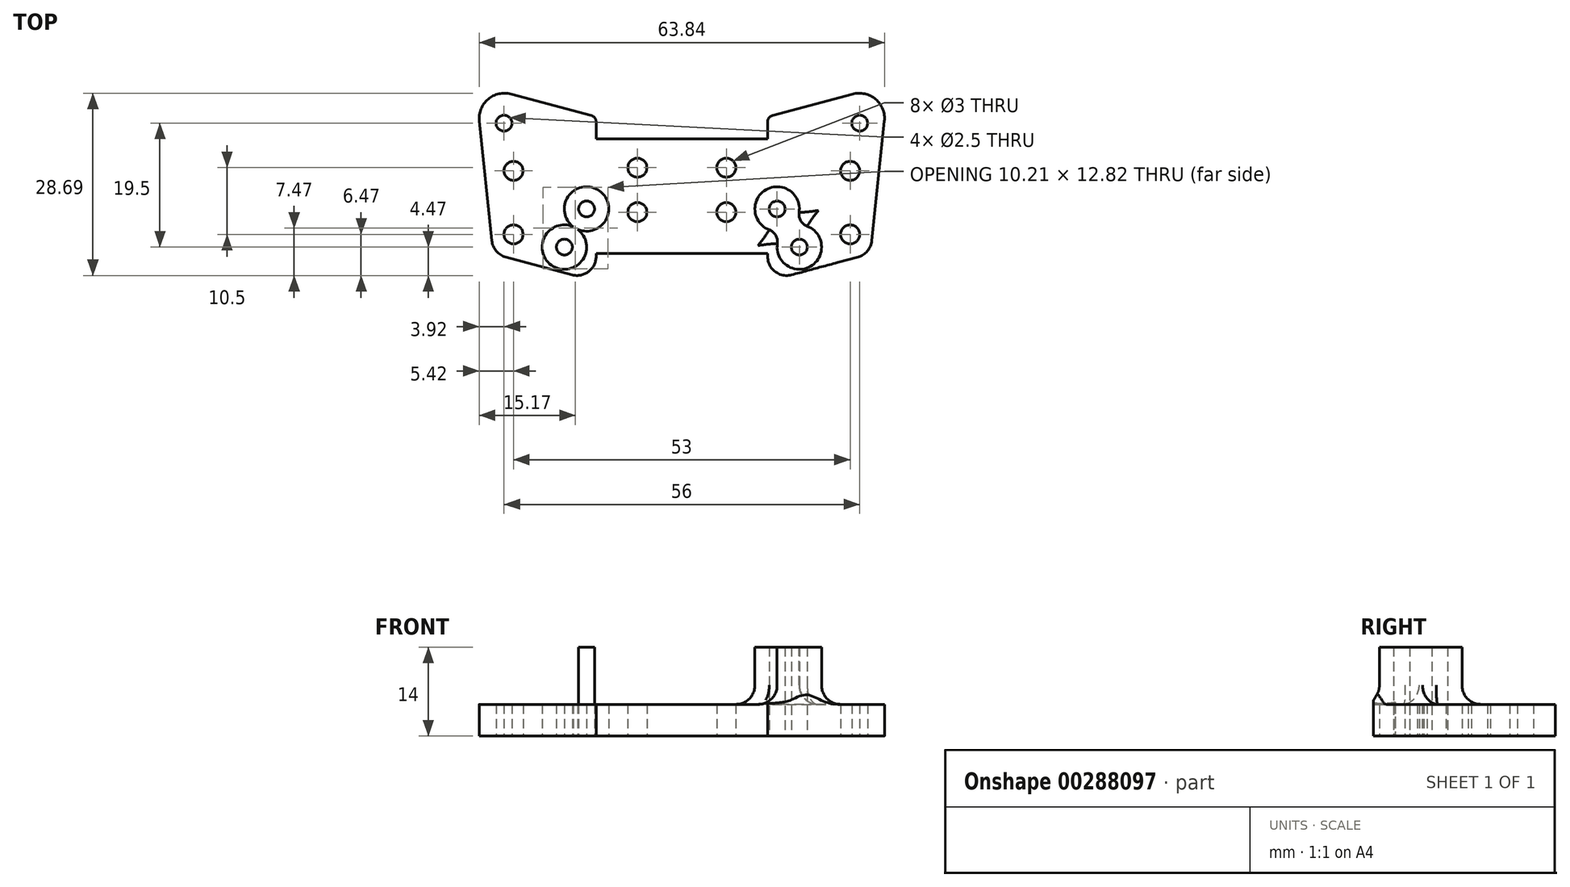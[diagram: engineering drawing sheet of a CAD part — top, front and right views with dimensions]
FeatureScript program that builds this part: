
annotation { "Feature Type Name" : "Feature", "Feature Type Description" : "" }
export const myFeature = defineFeature(function(context is Context, id is Id, definition is map)
    precondition{}
    {
        {
            var Q0;
            Q0=qCreatedBy(makeId("Top.planeOp"),FACE);
            var sketch = newSketch(context, id + "F0", { "sketchPlane" : qUnion([Q0])});
            skLineSegment(sketch, "E0", {"start": v(0, 0) * mm, "end": v(0, 21.8) * mm, "construction": true});
            skLineSegment(sketch, "E1", {"start": v(0, 0) * mm, "end": v(13.5, 0) * mm});
            skLineSegment(sketch, "E2", {"start": v(13.5, 0) * mm, "end": v(13.5, 2.73) * mm});
            skLineSegment(sketch, "E3", {"start": v(14.24, 3.7) * mm, "end": v(26.88, 7.09) * mm});
            skLineSegment(sketch, "E4", {"start": v(31.9, 2.8) * mm, "end": v(29.92, -15.99) * mm});
            skLineSegment(sketch, "E5", {"start": v(27.71, -18.57) * mm, "end": v(17.28, -21.37) * mm});
            skLineSegment(sketch, "E6", {"start": v(13.5, -18.47) * mm, "end": v(13.5, -18) * mm});
            skLineSegment(sketch, "E7", {"start": v(13.5, -18) * mm, "end": v(0, -18) * mm});
            skLineSegment(sketch, "E8", {"start": v(32.5, 8.6) * mm, "end": v(32.5, -12.43) * mm, "construction": true});
            skCircle(sketch, "E9", {"center": v(28, 2.5) * mm, "radius": 1.25 * mm});
            skPoint(sketch, "E10.visualSharp", {"position": v(32.5, 8.6) * mm});
            skArc(sketch, "E10.filletArc", {"start": v(31.9, 2.8) * mm, "mid": v(30.51, 6.26) * mm, "end": v(26.88, 7.09) * mm});
            skCircle(sketch, "E11", {"center": v(26.5, -5) * mm, "radius": 1.5 * mm});
            skCircle(sketch, "E12", {"center": v(26.5, -15) * mm, "radius": 1.5 * mm});
            skCircle(sketch, "E13", {"center": v(7, -4.5) * mm, "radius": 1.5 * mm});
            skCircle(sketch, "E14", {"center": v(7, -11.5) * mm, "radius": 1.5 * mm});
            skCircle(sketch, "E15", {"center": v(15, -11) * mm, "radius": 1.25 * mm});
            skCircle(sketch, "E16", {"center": v(18.5, -17) * mm, "radius": 1.25 * mm});
            skArc(sketch, "E17", {"start": v(17.12, -13.78) * mm, "mid": v(13.24, -7.98) * mm, "end": v(16.38, -14.22) * mm});
            skArc(sketch, "E18", {"start": v(16.38, -14.22) * mm, "mid": v(20.26, -20.02) * mm, "end": v(17.12, -13.78) * mm});
            skPoint(sketch, "E19.visualSharp", {"position": v(13.5, 3.5) * mm});
            skArc(sketch, "E19.filletArc", {"start": v(14.24, 3.7) * mm, "mid": v(13.7, 3.34) * mm, "end": v(13.5, 2.73) * mm});
            skPoint(sketch, "E20.visualSharp", {"position": v(29.7, -18.04) * mm});
            skArc(sketch, "E20.filletArc", {"start": v(27.71, -18.57) * mm, "mid": v(29.22, -17.62) * mm, "end": v(29.92, -15.99) * mm});
            skPoint(sketch, "E21.visualSharp", {"position": v(13.5, -22.38) * mm});
            skArc(sketch, "E21.filletArc", {"start": v(13.5, -18.47) * mm, "mid": v(14.67, -20.85) * mm, "end": v(17.28, -21.37) * mm});
            skCircle(sketch, "E22.MirrorC", {"center": v(-7, -4.5) * mm, "radius": 1.5 * mm});
            skCircle(sketch, "E23.MirrorC", {"center": v(-7, -11.5) * mm, "radius": 1.5 * mm});
            skCircle(sketch, "E24.MirrorC", {"center": v(-15, -11) * mm, "radius": 1.25 * mm});
            skArc(sketch, "E25.MirrorC", {"start": v(-17.12, -13.78) * mm, "mid": v(-13.24, -7.98) * mm, "end": v(-16.38, -14.22) * mm});
            skCircle(sketch, "E26.MirrorC", {"center": v(-18.5, -17) * mm, "radius": 1.25 * mm});
            skArc(sketch, "E27.MirrorC", {"start": v(-16.38, -14.22) * mm, "mid": v(-20.26, -20.02) * mm, "end": v(-17.12, -13.78) * mm});
            skCircle(sketch, "E28.MirrorC", {"center": v(-26.5, -15) * mm, "radius": 1.5 * mm});
            skCircle(sketch, "E29.MirrorC", {"center": v(-26.5, -5) * mm, "radius": 1.5 * mm});
            skCircle(sketch, "E30.MirrorC", {"center": v(-28, 2.5) * mm, "radius": 1.25 * mm});
            skLineSegment(sketch, "E31.MirrorCS", {"start": v(-13.5, -18) * mm, "end": v(0, -18) * mm});
            skLineSegment(sketch, "E32.MirrorCS", {"start": v(-13.5, -18.47) * mm, "end": v(-13.5, -18) * mm});
            skArc(sketch, "E33.MirrorCS", {"start": v(-13.5, -18.47) * mm, "mid": v(-14.67, -20.85) * mm, "end": v(-17.28, -21.37) * mm});
            skLineSegment(sketch, "E34.MirrorCS", {"start": v(-27.71, -18.57) * mm, "end": v(-17.28, -21.37) * mm});
            skArc(sketch, "E35.MirrorCS", {"start": v(-27.71, -18.57) * mm, "mid": v(-29.22, -17.62) * mm, "end": v(-29.92, -15.99) * mm});
            skLineSegment(sketch, "E36.MirrorCS", {"start": v(-31.9, 2.8) * mm, "end": v(-29.92, -15.99) * mm});
            skArc(sketch, "E37.MirrorCS", {"start": v(-31.9, 2.8) * mm, "mid": v(-30.51, 6.26) * mm, "end": v(-26.88, 7.09) * mm});
            skLineSegment(sketch, "E38.MirrorCS", {"start": v(-14.24, 3.7) * mm, "end": v(-26.88, 7.09) * mm});
            skArc(sketch, "E39.MirrorCS", {"start": v(-14.24, 3.7) * mm, "mid": v(-13.7, 3.34) * mm, "end": v(-13.5, 2.73) * mm});
            skLineSegment(sketch, "E40.MirrorCS", {"start": v(0, 0) * mm, "end": v(-13.5, 0) * mm});
            skLineSegment(sketch, "E41.MirrorCS", {"start": v(-13.5, 0) * mm, "end": v(-13.5, 2.73) * mm});
            skSolve(sketch);
        }
        {
            var Q0;
            Q0=makeQuery(id+"F0.imprint","IMPRINT",FACE,{"disambiguationData":[TD([[makeQuery(id+"F0.imprint","IMPRINT",EDGE,{"derivedFrom":sQuery(id+"F0.wireOp",EDGE,"E1")}),-1.0]])]});
            var Q1;
            Q1=makeQuery(id+"F0.imprint","IMPRINT",FACE,{"disambiguationData":[TD([[makeQuery(id+"F0.imprint","IMPRINT",EDGE,{"derivedFrom":sQuery(id+"F0.wireOp",EDGE,"E15")}),-1.0]])]});
            var Q2;
            Q2=makeQuery(id+"F0.imprint","IMPRINT",FACE,{"disambiguationData":[TD([[makeQuery(id+"F0.imprint","IMPRINT",EDGE,{"derivedFrom":sQuery(id+"F0.wireOp",EDGE,"E16")}),-1.0]])]});
            var Q3;
            Q3=makeQuery(id+"F0.imprint","IMPRINT",FACE,{"disambiguationData":[TD([[makeQuery(id+"F0.imprint","IMPRINT",EDGE,{"derivedFrom":sQuery(id+"F0.wireOp",EDGE,"E24.MirrorC")}),1.0]])]});
            var Q4;
            Q4=makeQuery(id+"F0.imprint","IMPRINT",FACE,{"disambiguationData":[TD([[makeQuery(id+"F0.imprint","IMPRINT",EDGE,{"derivedFrom":sQuery(id+"F0.wireOp",EDGE,"E26.MirrorC")}),1.0]])]});
            extrude(context, id + "F1", {"entities" : qUnion([Q0, Q1, Q2, Q3, Q4]), "depth" : 5 * mm});
        }
        {
            var Q0;
            Q0=makeQuery(id+"F0.imprint","IMPRINT",FACE,{"disambiguationData":[TD([[makeQuery(id+"F0.imprint","IMPRINT",EDGE,{"derivedFrom":sQuery(id+"F0.wireOp",EDGE,"E24.MirrorC")}),1.0]])]});
            var Q1;
            Q1=makeQuery(id+"F0.imprint","IMPRINT",FACE,{"disambiguationData":[TD([[makeQuery(id+"F0.imprint","IMPRINT",EDGE,{"derivedFrom":sQuery(id+"F0.wireOp",EDGE,"E15")}),-1.0]])]});
            extrude(context, id + "F2", {"entities" : qUnion([Q0, Q1]), "operationType" : NewBodyOperationType.ADD, "depth" : 14 * mm});
        }
        {
            var Q0;
            Q0=makeQuery(id+"F2.boolean.opBoolean","INTERSECT",EDGE,{"derivedFrom":[makeQuery(id+"F1.opExtrude","CAP_FACE",FACE,{"disambiguationData":[OSD([sQuery(id+"F0.wireOp",EDGE,"E1"),sQuery(id+"F0.wireOp",EDGE,"E2"),sQuery(id+"F0.wireOp",EDGE,"E3"),sQuery(id+"F0.wireOp",EDGE,"E4"),sQuery(id+"F0.wireOp",EDGE,"E5"),sQuery(id+"F0.wireOp",EDGE,"E6"),sQuery(id+"F0.wireOp",EDGE,"E7"),sQuery(id+"F0.wireOp",EDGE,"E9"),sQuery(id+"F0.wireOp",EDGE,"E10.filletArc"),sQuery(id+"F0.wireOp",EDGE,"E11"),sQuery(id+"F0.wireOp",EDGE,"E12"),sQuery(id+"F0.wireOp",EDGE,"E13"),sQuery(id+"F0.wireOp",EDGE,"E14"),sQuery(id+"F0.wireOp",EDGE,"E15"),sQuery(id+"F0.wireOp",EDGE,"E16"),sQuery(id+"F0.wireOp",EDGE,"E19.filletArc"),sQuery(id+"F0.wireOp",EDGE,"E20.filletArc"),sQuery(id+"F0.wireOp",EDGE,"E21.filletArc"),sQuery(id+"F0.wireOp",EDGE,"E22.MirrorC"),sQuery(id+"F0.wireOp",EDGE,"E23.MirrorC"),sQuery(id+"F0.wireOp",EDGE,"E24.MirrorC"),sQuery(id+"F0.wireOp",EDGE,"E26.MirrorC"),sQuery(id+"F0.wireOp",EDGE,"E28.MirrorC"),sQuery(id+"F0.wireOp",EDGE,"E29.MirrorC"),sQuery(id+"F0.wireOp",EDGE,"E30.MirrorC"),sQuery(id+"F0.wireOp",EDGE,"E31.MirrorCS"),sQuery(id+"F0.wireOp",EDGE,"E32.MirrorCS"),sQuery(id+"F0.wireOp",EDGE,"E33.MirrorCS"),sQuery(id+"F0.wireOp",EDGE,"E34.MirrorCS"),sQuery(id+"F0.wireOp",EDGE,"E35.MirrorCS"),sQuery(id+"F0.wireOp",EDGE,"E36.MirrorCS"),sQuery(id+"F0.wireOp",EDGE,"E37.MirrorCS"),sQuery(id+"F0.wireOp",EDGE,"E38.MirrorCS"),sQuery(id+"F0.wireOp",EDGE,"E39.MirrorCS"),sQuery(id+"F0.wireOp",EDGE,"E40.MirrorCS"),sQuery(id+"F0.wireOp",EDGE,"E41.MirrorCS")])],"isStart":false}),makeQuery(id+"F2.opExtrude","SWEPT_FACE",FACE,{"disambiguationData":[OSD([sQuery(id+"F0.wireOp",EDGE,"E25.MirrorC")])]})]});
            var Q1;
            Q1=makeQuery(id+"F2.boolean.opBoolean","INTERSECT",EDGE,{"derivedFrom":[makeQuery(id+"F1.opExtrude","CAP_FACE",FACE,{"disambiguationData":[OSD([sQuery(id+"F0.wireOp",EDGE,"E1"),sQuery(id+"F0.wireOp",EDGE,"E2"),sQuery(id+"F0.wireOp",EDGE,"E3"),sQuery(id+"F0.wireOp",EDGE,"E4"),sQuery(id+"F0.wireOp",EDGE,"E5"),sQuery(id+"F0.wireOp",EDGE,"E6"),sQuery(id+"F0.wireOp",EDGE,"E7"),sQuery(id+"F0.wireOp",EDGE,"E9"),sQuery(id+"F0.wireOp",EDGE,"E10.filletArc"),sQuery(id+"F0.wireOp",EDGE,"E11"),sQuery(id+"F0.wireOp",EDGE,"E12"),sQuery(id+"F0.wireOp",EDGE,"E13"),sQuery(id+"F0.wireOp",EDGE,"E14"),sQuery(id+"F0.wireOp",EDGE,"E15"),sQuery(id+"F0.wireOp",EDGE,"E16"),sQuery(id+"F0.wireOp",EDGE,"E19.filletArc"),sQuery(id+"F0.wireOp",EDGE,"E20.filletArc"),sQuery(id+"F0.wireOp",EDGE,"E21.filletArc"),sQuery(id+"F0.wireOp",EDGE,"E22.MirrorC"),sQuery(id+"F0.wireOp",EDGE,"E23.MirrorC"),sQuery(id+"F0.wireOp",EDGE,"E24.MirrorC"),sQuery(id+"F0.wireOp",EDGE,"E26.MirrorC"),sQuery(id+"F0.wireOp",EDGE,"E28.MirrorC"),sQuery(id+"F0.wireOp",EDGE,"E29.MirrorC"),sQuery(id+"F0.wireOp",EDGE,"E30.MirrorC"),sQuery(id+"F0.wireOp",EDGE,"E31.MirrorCS"),sQuery(id+"F0.wireOp",EDGE,"E32.MirrorCS"),sQuery(id+"F0.wireOp",EDGE,"E33.MirrorCS"),sQuery(id+"F0.wireOp",EDGE,"E34.MirrorCS"),sQuery(id+"F0.wireOp",EDGE,"E35.MirrorCS"),sQuery(id+"F0.wireOp",EDGE,"E36.MirrorCS"),sQuery(id+"F0.wireOp",EDGE,"E37.MirrorCS"),sQuery(id+"F0.wireOp",EDGE,"E38.MirrorCS"),sQuery(id+"F0.wireOp",EDGE,"E39.MirrorCS"),sQuery(id+"F0.wireOp",EDGE,"E40.MirrorCS"),sQuery(id+"F0.wireOp",EDGE,"E41.MirrorCS")])],"isStart":false}),makeQuery(id+"F2.opExtrude","SWEPT_FACE",FACE,{"disambiguationData":[OSD([sQuery(id+"F0.wireOp",EDGE,"E27.MirrorC")])]})]});
            var Q2;
            Q2=makeQuery(id+"F2.boolean.opBoolean","INTERSECT",EDGE,{"derivedFrom":[makeQuery(id+"F1.opExtrude","CAP_FACE",FACE,{"disambiguationData":[OSD([sQuery(id+"F0.wireOp",EDGE,"E1"),sQuery(id+"F0.wireOp",EDGE,"E2"),sQuery(id+"F0.wireOp",EDGE,"E3"),sQuery(id+"F0.wireOp",EDGE,"E4"),sQuery(id+"F0.wireOp",EDGE,"E5"),sQuery(id+"F0.wireOp",EDGE,"E6"),sQuery(id+"F0.wireOp",EDGE,"E7"),sQuery(id+"F0.wireOp",EDGE,"E9"),sQuery(id+"F0.wireOp",EDGE,"E10.filletArc"),sQuery(id+"F0.wireOp",EDGE,"E11"),sQuery(id+"F0.wireOp",EDGE,"E12"),sQuery(id+"F0.wireOp",EDGE,"E13"),sQuery(id+"F0.wireOp",EDGE,"E14"),sQuery(id+"F0.wireOp",EDGE,"E15"),sQuery(id+"F0.wireOp",EDGE,"E16"),sQuery(id+"F0.wireOp",EDGE,"E19.filletArc"),sQuery(id+"F0.wireOp",EDGE,"E20.filletArc"),sQuery(id+"F0.wireOp",EDGE,"E21.filletArc"),sQuery(id+"F0.wireOp",EDGE,"E22.MirrorC"),sQuery(id+"F0.wireOp",EDGE,"E23.MirrorC"),sQuery(id+"F0.wireOp",EDGE,"E24.MirrorC"),sQuery(id+"F0.wireOp",EDGE,"E26.MirrorC"),sQuery(id+"F0.wireOp",EDGE,"E28.MirrorC"),sQuery(id+"F0.wireOp",EDGE,"E29.MirrorC"),sQuery(id+"F0.wireOp",EDGE,"E30.MirrorC"),sQuery(id+"F0.wireOp",EDGE,"E31.MirrorCS"),sQuery(id+"F0.wireOp",EDGE,"E32.MirrorCS"),sQuery(id+"F0.wireOp",EDGE,"E33.MirrorCS"),sQuery(id+"F0.wireOp",EDGE,"E34.MirrorCS"),sQuery(id+"F0.wireOp",EDGE,"E35.MirrorCS"),sQuery(id+"F0.wireOp",EDGE,"E36.MirrorCS"),sQuery(id+"F0.wireOp",EDGE,"E37.MirrorCS"),sQuery(id+"F0.wireOp",EDGE,"E38.MirrorCS"),sQuery(id+"F0.wireOp",EDGE,"E39.MirrorCS"),sQuery(id+"F0.wireOp",EDGE,"E40.MirrorCS"),sQuery(id+"F0.wireOp",EDGE,"E41.MirrorCS")])],"isStart":false}),makeQuery(id+"F2.opExtrude","SWEPT_FACE",FACE,{"disambiguationData":[OSD([sQuery(id+"F0.wireOp",EDGE,"E17")])]})]});
            var Q3;
            Q3=makeQuery(id+"F2.boolean.opBoolean","INTERSECT",EDGE,{"derivedFrom":[makeQuery(id+"F1.opExtrude","CAP_FACE",FACE,{"disambiguationData":[OSD([sQuery(id+"F0.wireOp",EDGE,"E1"),sQuery(id+"F0.wireOp",EDGE,"E2"),sQuery(id+"F0.wireOp",EDGE,"E3"),sQuery(id+"F0.wireOp",EDGE,"E4"),sQuery(id+"F0.wireOp",EDGE,"E5"),sQuery(id+"F0.wireOp",EDGE,"E6"),sQuery(id+"F0.wireOp",EDGE,"E7"),sQuery(id+"F0.wireOp",EDGE,"E9"),sQuery(id+"F0.wireOp",EDGE,"E10.filletArc"),sQuery(id+"F0.wireOp",EDGE,"E11"),sQuery(id+"F0.wireOp",EDGE,"E12"),sQuery(id+"F0.wireOp",EDGE,"E13"),sQuery(id+"F0.wireOp",EDGE,"E14"),sQuery(id+"F0.wireOp",EDGE,"E15"),sQuery(id+"F0.wireOp",EDGE,"E16"),sQuery(id+"F0.wireOp",EDGE,"E19.filletArc"),sQuery(id+"F0.wireOp",EDGE,"E20.filletArc"),sQuery(id+"F0.wireOp",EDGE,"E21.filletArc"),sQuery(id+"F0.wireOp",EDGE,"E22.MirrorC"),sQuery(id+"F0.wireOp",EDGE,"E23.MirrorC"),sQuery(id+"F0.wireOp",EDGE,"E24.MirrorC"),sQuery(id+"F0.wireOp",EDGE,"E26.MirrorC"),sQuery(id+"F0.wireOp",EDGE,"E28.MirrorC"),sQuery(id+"F0.wireOp",EDGE,"E29.MirrorC"),sQuery(id+"F0.wireOp",EDGE,"E30.MirrorC"),sQuery(id+"F0.wireOp",EDGE,"E31.MirrorCS"),sQuery(id+"F0.wireOp",EDGE,"E32.MirrorCS"),sQuery(id+"F0.wireOp",EDGE,"E33.MirrorCS"),sQuery(id+"F0.wireOp",EDGE,"E34.MirrorCS"),sQuery(id+"F0.wireOp",EDGE,"E35.MirrorCS"),sQuery(id+"F0.wireOp",EDGE,"E36.MirrorCS"),sQuery(id+"F0.wireOp",EDGE,"E37.MirrorCS"),sQuery(id+"F0.wireOp",EDGE,"E38.MirrorCS"),sQuery(id+"F0.wireOp",EDGE,"E39.MirrorCS"),sQuery(id+"F0.wireOp",EDGE,"E40.MirrorCS"),sQuery(id+"F0.wireOp",EDGE,"E41.MirrorCS")])],"isStart":false}),makeQuery(id+"F2.opExtrude","SWEPT_FACE",FACE,{"disambiguationData":[OSD([sQuery(id+"F0.wireOp",EDGE,"E18")])]})]});
            fillet(context, id + "F3", {"entities" : qUnion([Q0, Q1, Q2, Q3]), "radius" : 3 * mm, "tangentPropagation" : true, "allowEdgeOverflow" : false});
        }
        {
            var Q0;
            {var subQ0=sQuery(id+"F0.wireOp",EDGE,"E27.MirrorC");var subQ1=sQuery(id+"F0.wireOp",EDGE,"E25.MirrorC");Q0=makeQuery(id+"F2.opExtrude","SWEPT_EDGE",EDGE,{"disambiguationData":[OSD([subQ1,subQ0]),TDD([makeQuery(id+"F0.imprint","INTERSECT",VERTEX,{"disambiguationData":[OD(1.0)],"derivedFrom":[subQ1,subQ0]})])]});}
            var Q1;
            {var subQ0=sQuery(id+"F0.wireOp",EDGE,"E27.MirrorC");var subQ1=sQuery(id+"F0.wireOp",EDGE,"E25.MirrorC");Q1=makeQuery(id+"F2.opExtrude","SWEPT_EDGE",EDGE,{"disambiguationData":[OSD([subQ1,subQ0]),TDD([makeQuery(id+"F0.imprint","INTERSECT",VERTEX,{"disambiguationData":[OD(0.0)],"derivedFrom":[subQ1,subQ0]})])]});}
            var Q2;
            {var subQ0=sQuery(id+"F0.wireOp",EDGE,"E18");var subQ1=sQuery(id+"F0.wireOp",EDGE,"E17");Q2=makeQuery(id+"F2.opExtrude","SWEPT_EDGE",EDGE,{"disambiguationData":[OSD([subQ1,subQ0]),TDD([makeQuery(id+"F0.imprint","INTERSECT",VERTEX,{"disambiguationData":[OD(0.0)],"derivedFrom":[subQ1,subQ0]})])]});}
            var Q3;
            {var subQ0=sQuery(id+"F0.wireOp",EDGE,"E18");var subQ1=sQuery(id+"F0.wireOp",EDGE,"E17");Q3=makeQuery(id+"F2.opExtrude","SWEPT_EDGE",EDGE,{"disambiguationData":[OSD([subQ1,subQ0]),TDD([makeQuery(id+"F0.imprint","INTERSECT",VERTEX,{"disambiguationData":[OD(1.0)],"derivedFrom":[subQ1,subQ0]})])]});}
            fillet(context, id + "F4", {"entities" : qUnion([Q0, Q1, Q2, Q3]), "radius" : 2 * mm, "tangentPropagation" : true, "allowEdgeOverflow" : false});
        }
    });
